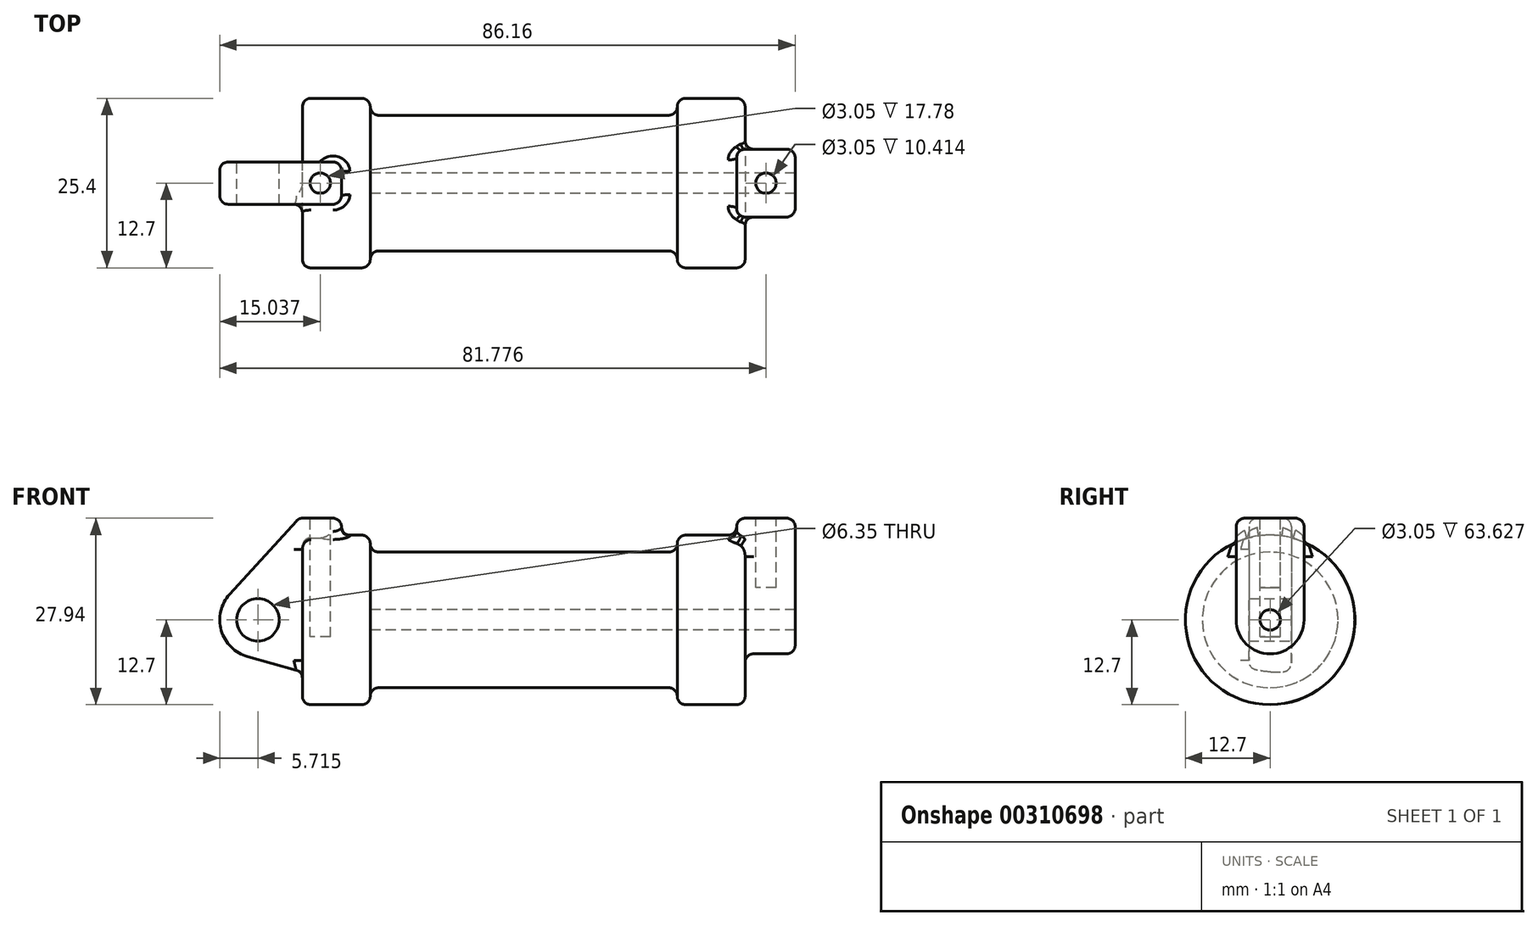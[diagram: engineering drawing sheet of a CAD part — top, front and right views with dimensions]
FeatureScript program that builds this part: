
annotation { "Feature Type Name" : "Feature", "Feature Type Description" : "" }
export const myFeature = defineFeature(function(context is Context, id is Id, definition is map)
    precondition{}
    {
        {
            var Q0;
            Q0=qCreatedBy(makeId("Front.planeOp"),FACE);
            var sketch = newSketch(context, id + "F0", { "sketchPlane" : qUnion([Q0])});
            skLineSegment(sketch, "E0", {"start": v(0, 0) * mm, "end": v(0, 12.7) * mm});
            skLineSegment(sketch, "E1", {"start": v(0, 12.7) * mm, "end": v(10.16, 12.7) * mm});
            skLineSegment(sketch, "E2", {"start": v(10.16, 12.7) * mm, "end": v(10.16, 10.16) * mm});
            skLineSegment(sketch, "E3", {"start": v(10.16, 10.16) * mm, "end": v(56.13, 10.16) * mm});
            skLineSegment(sketch, "E4", {"start": v(56.13, 10.16) * mm, "end": v(56.13, 12.7) * mm});
            skLineSegment(sketch, "E5", {"start": v(56.13, 12.7) * mm, "end": v(66.3, 12.7) * mm});
            skLineSegment(sketch, "E6", {"start": v(66.3, 12.7) * mm, "end": v(66.3, 0) * mm});
            skLineSegment(sketch, "E7", {"start": v(66.3, 0) * mm, "end": v(0, 0) * mm});
            skLineSegment(sketch, "E8", {"start": v(5.84, 15.24) * mm, "end": v(-0.5, 15.24) * mm});
            skLineSegment(sketch, "E9", {"start": v(-0.5, 15.24) * mm, "end": v(-10.88, 3.85) * mm});
            skLineSegment(sketch, "E10", {"start": v(0, 0) * mm, "end": v(-6.65, 0) * mm});
            skCircle(sketch, "E11", {"center": v(-6.65, 0) * mm, "radius": 5.72 * mm});
            skCircle(sketch, "E12", {"center": v(-6.65, 0) * mm, "radius": 3.18 * mm});
            skLineSegment(sketch, "E13", {"start": v(5.84, 15.24) * mm, "end": v(5.84, -9.4) * mm});
            skLineSegment(sketch, "E14", {"start": v(5.84, -9.4) * mm, "end": v(-8.18, -5.5) * mm});
            skSolve(sketch);
        }
        {
            var Q0;
            {var subQ0=sQuery(id+"F0.wireOp",EDGE,"E2");Q0=makeQuery(id+"F0.imprint","IMPRINT",FACE,{"disambiguationData":[TD([[makeQuery(id+"F0.imprint","IMPRINT",EDGE,{"derivedFrom":subQ0}),-1.0]])]});}
            var Q1;
            {var subQ0=sQuery(id+"F0.wireOp",EDGE,"E0");Q1=makeQuery(id+"F0.imprint","IMPRINT",FACE,{"disambiguationData":[TD([[makeQuery(id+"F0.imprint","IMPRINT",EDGE,{"derivedFrom":subQ0}),-1.0]])]});}
            var Q2;
            Q2=sQuery(id+"F0.wireOp",EDGE,"E7");
            revolve(context, id + "F1", {"entities" : qUnion([Q0, Q1]), "axis" : qUnion([Q2]), "revolveType" : RevolveType.FULL});
        }
        {
            var Q0;
            {var subQ1=sQuery(id+"F0.wireOp",EDGE,"E0");Q0=makeQuery(id+"F0.imprint","IMPRINT",FACE,{"disambiguationData":[TD([[makeQuery(id+"F0.imprint","IMPRINT",EDGE,{"derivedFrom":subQ1}),1.0]])]});}
            var Q1;
            {var subQ0=sQuery(id+"F0.wireOp",EDGE,"E0");Q1=makeQuery(id+"F0.imprint","IMPRINT",FACE,{"disambiguationData":[TD([[makeQuery(id+"F0.imprint","IMPRINT",EDGE,{"derivedFrom":subQ0}),-1.0]])]});}
            var Q2;
            {var subQ0=sQuery(id+"F0.wireOp",EDGE,"E14");Q2=makeQuery(id+"F0.imprint","IMPRINT",FACE,{"disambiguationData":[TD([[makeQuery(id+"F0.imprint","IMPRINT",EDGE,{"derivedFrom":subQ0}),-1.0]])]});}
            var Q3;
            {var subQ5=sQuery(id+"F0.wireOp",EDGE,"E12");Q3=makeQuery(id+"F0.imprint","IMPRINT",FACE,{"disambiguationData":[TD([[makeQuery(id+"F0.imprint","IMPRINT",EDGE,{"derivedFrom":subQ5}),-1.0]])]});}
            var Q4;
            Q4=sQuery(id+"F0.wireOp",EDGE,"E9");
            var Q5;
            Q5=sQuery(id+"F0.wireOp",EDGE,"E8");
            var Q6;
            Q6=sQuery(id+"F0.wireOp",EDGE,"E13");
            var Q7;
            Q7=sQuery(id+"F0.wireOp",EDGE,"E14");
            var Q8;
            Q8=sQuery(id+"F0.wireOp",EDGE,"E11");
            extrude(context, id + "F2", {"entities" : qUnion([Q0, Q1, Q2, Q3]), "operationType" : NewBodyOperationType.ADD, "surfaceEntities" : qUnion([Q4, Q5, Q6, Q7, Q8]), "endBound" : BoundingType.SYMMETRIC, "depth" : 6.35 * mm});
        }
        {
            var Q0;
            Q0=makeQuery(id+"F1.opRevolve","SWEPT_FACE",FACE,{"disambiguationData":[OSD([sQuery(id+"F0.wireOp",EDGE,"E6")])]});
            var sketch = newSketch(context, id + "F3", { "sketchPlane" : qUnion([Q0])});
            skCircle(sketch, "E15.0", {"center": v(0, 0) * mm, "radius": 12.7 * mm, "construction": true});
            skCircle(sketch, "E16", {"center": v(0, 0) * mm, "radius": 1.52 * mm});
            skCircle(sketch, "E17", {"center": v(0, 0) * mm, "radius": 5.08 * mm});
            skLineSegment(sketch, "E18", {"start": v(5.08, 0) * mm, "end": v(5.08, 15.24) * mm});
            skLineSegment(sketch, "E19", {"start": v(5.08, 15.24) * mm, "end": v(-5.08, 15.24) * mm});
            skLineSegment(sketch, "E20", {"start": v(-5.08, 15.24) * mm, "end": v(-5.08, 0) * mm});
            skSolve(sketch);
        }
        {
            var Q0;
            {var subQ0=sQuery(id+"F3.wireOp",EDGE,"E19");Q0=makeQuery(id+"F3.imprint","IMPRINT",FACE,{"disambiguationData":[TD([[makeQuery(id+"F3.imprint","IMPRINT",EDGE,{"derivedFrom":subQ0}),1.0]])]});}
            var Q1;
            {var subQ0=sQuery(id+"F3.wireOp",EDGE,"E18");var subQ1=sQuery(id+"F3.wireOp",EDGE,"E17");var subQ2=makeQuery(id+"F3.imprint","INTERSECT",VERTEX,{"derivedFrom":[subQ1,subQ0]});Q1=makeQuery(id+"F3.imprint","IMPRINT",FACE,{"disambiguationData":[TD([[makeQuery(id+"F3.imprint","IMPRINT",EDGE,{"disambiguationData":[TD([[subQ2,-1.0]])],"derivedFrom":subQ1}),-1.0]])]});}
            var Q2;
            Q2=makeQuery(id+"F3.imprint","IMPRINT",FACE,{"disambiguationData":[TD([[makeQuery(id+"F3.imprint","IMPRINT",EDGE,{"derivedFrom":sQuery(id+"F3.wireOp",EDGE,"E16")}),-1.0]])]});
            extrude(context, id + "F4", {"entities" : qUnion([Q0, Q1, Q2]), "operationType" : NewBodyOperationType.ADD, "depth" : 7.5 * mm, "hasSecondDirection" : true, "secondDirectionOppositeDirection" : true, "secondDirectionDepth" : 1.27 * mm});
        }
        {
            var Q0;
            Q0=makeQuery(id+"F4.boolean.opBoolean","SPLIT",FACE,{"disambiguationData":[TD([makeQuery(id+"F4.opExtrude","SWEPT_FACE",FACE,{"disambiguationData":[OSD([sQuery(id+"F3.wireOp",EDGE,"E16")])]})])],"derivedFrom":makeQuery(id+"F1.opRevolve","SWEPT_FACE",FACE,{"disambiguationData":[OSD([sQuery(id+"F0.wireOp",EDGE,"E6")])]})});
            var Q1;
            Q1=makeQuery(id+"F1.opRevolve","SWEPT_FACE",FACE,{"disambiguationData":[OSD([sQuery(id+"F0.wireOp",EDGE,"E2")])]});
            extrude(context, id + "F5", {"entities" : qUnion([Q0]), "operationType" : NewBodyOperationType.REMOVE, "endBound" : BoundingType.UP_TO_SURFACE, "oppositeDirection" : true, "endBoundEntityFace" : qUnion([Q1]), "depth" : 25.4 * mm});
        }
        {
            var Q0;
            Q0=makeQuery(id+"F2.opExtrude","SWEPT_FACE",FACE,{"disambiguationData":[OSD([sQuery(id+"F0.wireOp",EDGE,"E8")])]});
            var sketch = newSketch(context, id + "F6", { "sketchPlane" : qUnion([Q0])});
            skCircle(sketch, "E21", {"center": v(2.67, 0) * mm, "radius": 1.52 * mm});
            skSolve(sketch);
        }
        {
            var Q0;
            Q0=makeQuery(id+"F4.opExtrude","SWEPT_FACE",FACE,{"disambiguationData":[OSD([sQuery(id+"F3.wireOp",EDGE,"E19")])]});
            var sketch = newSketch(context, id + "F7", { "sketchPlane" : qUnion([Q0])});
            skCircle(sketch, "E22", {"center": v(69.4, 0) * mm, "radius": 1.52 * mm});
            skSolve(sketch);
        }
        {
            var Q0;
            Q0=makeQuery(id+"F6.imprint","IMPRINT",FACE,{"disambiguationData":[TD([[makeQuery(id+"F6.imprint","IMPRINT",EDGE,{"derivedFrom":sQuery(id+"F6.wireOp",EDGE,"E21")}),1.0]])]});
            var Q1;
            Q1=sQuery(id+"F6.wireOp",EDGE,"E21");
            extrude(context, id + "F8", {"entities" : qUnion([Q0]), "operationType" : NewBodyOperationType.REMOVE, "surfaceEntities" : qUnion([Q1]), "oppositeDirection" : true, "depth" : 17.78 * mm});
        }
        {
            var Q0;
            Q0=makeQuery(id+"F7.imprint","IMPRINT",FACE,{"disambiguationData":[TD([[makeQuery(id+"F7.imprint","IMPRINT",EDGE,{"derivedFrom":sQuery(id+"F7.wireOp",EDGE,"E22")}),1.0]])]});
            var Q1;
            Q1=sQuery(id+"F7.wireOp",EDGE,"E22");
            extrude(context, id + "F9", {"entities" : qUnion([Q0]), "operationType" : NewBodyOperationType.REMOVE, "surfaceEntities" : qUnion([Q1]), "oppositeDirection" : true, "depth" : 10.4 * mm});
        }
        {
            var Q0;
            Q0=makeQuery(id+"F1.opRevolve","SWEPT_FACE",FACE,{"disambiguationData":[OSD([sQuery(id+"F0.wireOp",EDGE,"E3")])]});
            var Q1;
            Q1=makeQuery(id+"F1.opRevolve","SWEPT_EDGE",EDGE,{"disambiguationData":[OSD([sQuery(id+"F0.wireOp",EDGE,"E1"),sQuery(id+"F0.wireOp",EDGE,"E2")])]});
            var Q2;
            Q2=makeQuery(id+"F1.opRevolve","SWEPT_EDGE",EDGE,{"disambiguationData":[OSD([sQuery(id+"F0.wireOp",EDGE,"E0"),sQuery(id+"F0.wireOp",EDGE,"E1")])]});
            var Q3;
            Q3=makeQuery(id+"F1.opRevolve","SWEPT_EDGE",EDGE,{"disambiguationData":[OSD([sQuery(id+"F0.wireOp",EDGE,"E4"),sQuery(id+"F0.wireOp",EDGE,"E5")])]});
            var Q4;
            Q4=makeQuery(id+"F1.opRevolve","SWEPT_EDGE",EDGE,{"disambiguationData":[OSD([sQuery(id+"F0.wireOp",EDGE,"E5"),sQuery(id+"F0.wireOp",EDGE,"E6")])]});
            fillet(context, id + "F10", {"entities" : qUnion([Q0, Q1, Q2, Q3, Q4]), "radius" : 1.27 * mm, "tangentPropagation" : true, "allowEdgeOverflow" : false});
        }
        {
            var Q0;
            Q0=makeQuery(id+"F4.boolean.opBoolean","INTERSECT",EDGE,{"derivedFrom":[makeQuery(id+"F1.opRevolve","SWEPT_FACE",FACE,{"disambiguationData":[OSD([sQuery(id+"F0.wireOp",EDGE,"E5")])]}),makeQuery(id+"F4.opExtrude","CAP_FACE",FACE,{"disambiguationData":[OSD([sQuery(id+"F3.wireOp",EDGE,"E16"),sQuery(id+"F3.wireOp",EDGE,"E17"),sQuery(id+"F3.wireOp",EDGE,"E18"),sQuery(id+"F3.wireOp",EDGE,"E19"),sQuery(id+"F3.wireOp",EDGE,"E20")])],"isStart":true})]});
            var Q1;
            Q1=makeQuery(id+"F10.opFillet","BLEND_EDGE",EDGE,{"blendedFrom":[makeQuery(id+"F1.opRevolve","SWEPT_EDGE",EDGE,{"disambiguationData":[OSD([sQuery(id+"F0.wireOp",EDGE,"E5"),sQuery(id+"F0.wireOp",EDGE,"E6")])]}),makeQuery(id+"F4.opExtrude","SWEPT_FACE",FACE,{"disambiguationData":[OSD([sQuery(id+"F3.wireOp",EDGE,"E20")])]})],"blendedInto":[makeQuery(id+"F4.opExtrude","SWEPT_FACE",FACE,{"disambiguationData":[OSD([sQuery(id+"F3.wireOp",EDGE,"E20")])]})]});
            var Q2;
            Q2=makeQuery(id+"F4.opExtrude","CAP_EDGE",EDGE,{"disambiguationData":[OSD([sQuery(id+"F3.wireOp",EDGE,"E20")])],"isStart":false});
            var Q3;
            Q3=makeQuery(id+"F4.opExtrude","SWEPT_EDGE",EDGE,{"disambiguationData":[OSD([sQuery(id+"F3.wireOp",EDGE,"E19"),sQuery(id+"F3.wireOp",EDGE,"E20")])]});
            var Q4;
            Q4=makeQuery(id+"F4.opExtrude","CAP_EDGE",EDGE,{"disambiguationData":[OSD([sQuery(id+"F3.wireOp",EDGE,"E19")])],"isStart":true});
            var Q5;
            Q5=makeQuery(id+"F4.opExtrude","SWEPT_EDGE",EDGE,{"disambiguationData":[OSD([sQuery(id+"F3.wireOp",EDGE,"E18"),sQuery(id+"F3.wireOp",EDGE,"E19")])]});
            var Q6;
            Q6=makeQuery(id+"F4.opExtrude","CAP_EDGE",EDGE,{"disambiguationData":[OSD([sQuery(id+"F3.wireOp",EDGE,"E19")])],"isStart":false});
            var Q7;
            Q7=makeQuery(id+"F4.opExtrude","CAP_EDGE",EDGE,{"disambiguationData":[OSD([sQuery(id+"F3.wireOp",EDGE,"E20")])],"isStart":true});
            var Q8;
            Q8=makeQuery(id+"F4.opExtrude","CAP_EDGE",EDGE,{"disambiguationData":[OSD([sQuery(id+"F3.wireOp",EDGE,"E18")])],"isStart":true});
            fillet(context, id + "F11", {"entities" : qUnion([Q0, Q1, Q2, Q3, Q4, Q5, Q6, Q7, Q8]), "radius" : 1.27 * mm, "tangentPropagation" : true, "allowEdgeOverflow" : false});
        }
        {
            var Q0;
            Q0=makeQuery(id+"F2.boolean.opBoolean","INTERSECT",EDGE,{"derivedFrom":[makeQuery(id+"F1.opRevolve","SWEPT_FACE",FACE,{"disambiguationData":[OSD([sQuery(id+"F0.wireOp",EDGE,"E1")])]}),makeQuery(id+"F2.opExtrude","SWEPT_FACE",FACE,{"disambiguationData":[OSD([sQuery(id+"F0.wireOp",EDGE,"E13")])]})]});
            var Q1;
            Q1=makeQuery(id+"F2.boolean.opBoolean","INTERSECT",EDGE,{"derivedFrom":[makeQuery(id+"F1.opRevolve","SWEPT_FACE",FACE,{"disambiguationData":[OSD([sQuery(id+"F0.wireOp",EDGE,"E1")])]}),makeQuery(id+"F2.opExtrude","CAP_FACE",FACE,{"disambiguationData":[OSD([sQuery(id+"F0.wireOp",EDGE,"E8"),sQuery(id+"F0.wireOp",EDGE,"E9"),sQuery(id+"F0.wireOp",EDGE,"E11"),sQuery(id+"F0.wireOp",EDGE,"E12"),sQuery(id+"F0.wireOp",EDGE,"E13"),sQuery(id+"F0.wireOp",EDGE,"E14")])],"isStart":false})]});
            var Q2;
            Q2=makeQuery(id+"F2.opExtrude","CAP_EDGE",EDGE,{"disambiguationData":[OSD([sQuery(id+"F0.wireOp",EDGE,"E13")])],"isStart":false});
            var Q3;
            Q3=makeQuery(id+"F2.opExtrude","CAP_EDGE",EDGE,{"disambiguationData":[OSD([sQuery(id+"F0.wireOp",EDGE,"E13")])],"isStart":true});
            var Q4;
            Q4=makeQuery(id+"F2.opExtrude","CAP_EDGE",EDGE,{"disambiguationData":[OSD([sQuery(id+"F0.wireOp",EDGE,"E8")])],"isStart":true});
            var Q5;
            Q5=makeQuery(id+"F2.opExtrude","CAP_EDGE",EDGE,{"disambiguationData":[OSD([sQuery(id+"F0.wireOp",EDGE,"E8")])],"isStart":false});
            var Q6;
            Q6=makeQuery(id+"F2.opExtrude","CAP_EDGE",EDGE,{"disambiguationData":[OSD([sQuery(id+"F0.wireOp",EDGE,"E9")])],"isStart":false});
            var Q7;
            Q7=makeQuery(id+"F2.opExtrude","CAP_EDGE",EDGE,{"disambiguationData":[OSD([sQuery(id+"F0.wireOp",EDGE,"E9")])],"isStart":true});
            var Q8;
            Q8=makeQuery(id+"F2.opExtrude","SWEPT_EDGE",EDGE,{"disambiguationData":[OSD([sQuery(id+"F0.wireOp",EDGE,"E8"),sQuery(id+"F0.wireOp",EDGE,"E9")])]});
            var Q9;
            Q9=makeQuery(id+"F2.opExtrude","SWEPT_EDGE",EDGE,{"disambiguationData":[OSD([sQuery(id+"F0.wireOp",EDGE,"E8"),sQuery(id+"F0.wireOp",EDGE,"E13")])]});
            fillet(context, id + "F12", {"entities" : qUnion([Q0, Q1, Q2, Q3, Q4, Q5, Q6, Q7, Q8, Q9]), "radius" : 1.27 * mm, "tangentPropagation" : true, "allowEdgeOverflow" : false});
        }
    });
